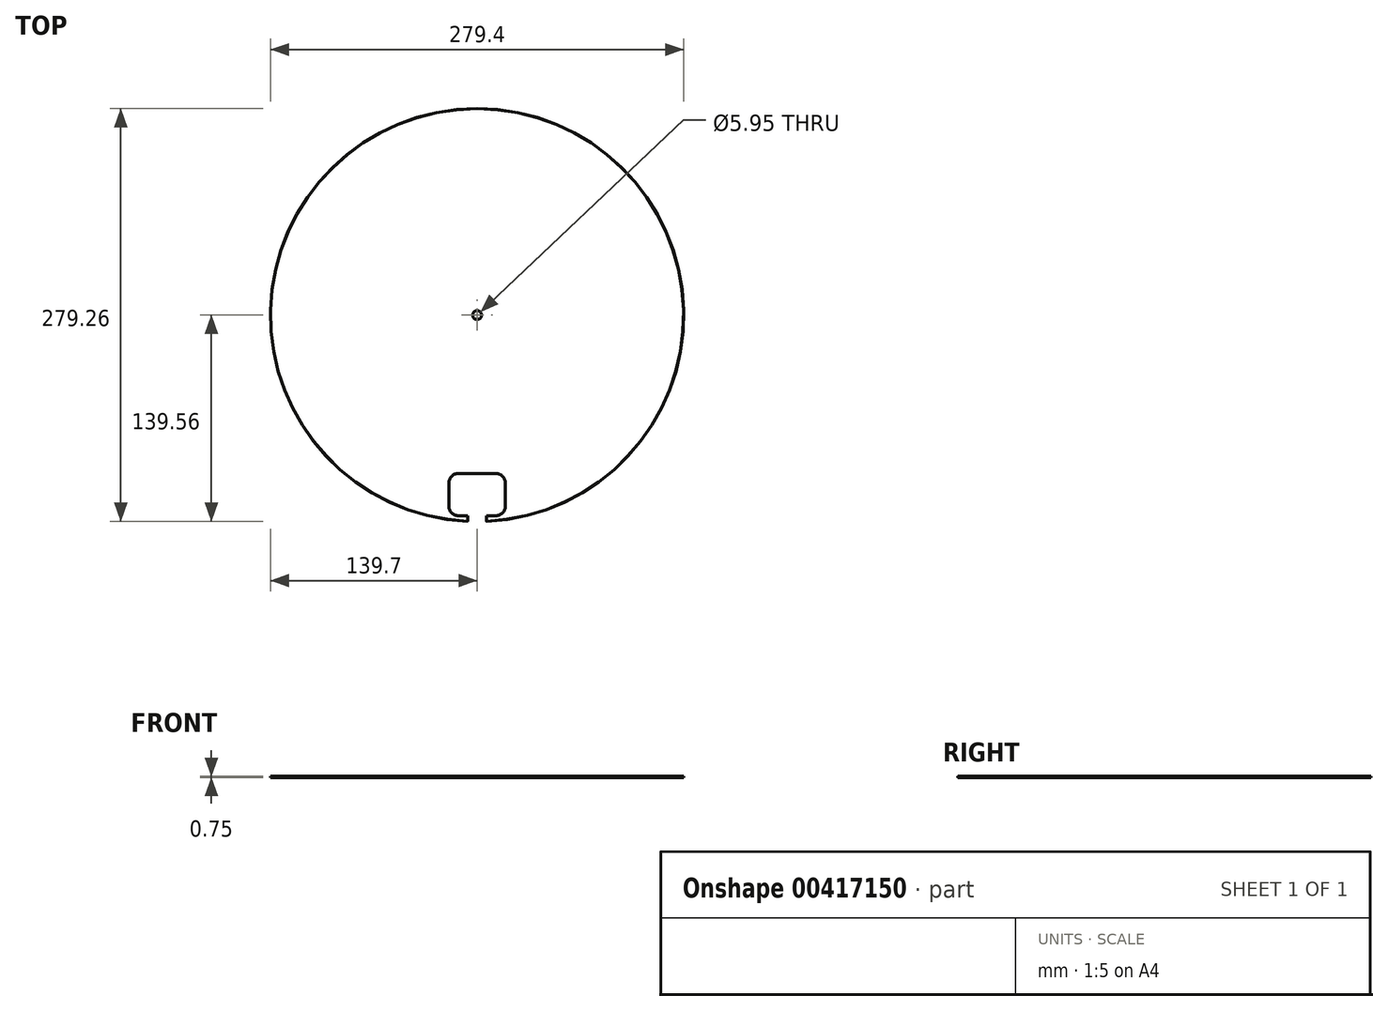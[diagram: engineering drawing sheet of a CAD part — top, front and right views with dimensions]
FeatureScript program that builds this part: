
annotation { "Feature Type Name" : "Feature", "Feature Type Description" : "" }
export const myFeature = defineFeature(function(context is Context, id is Id, definition is map)
    precondition{}
    {
        {
            assignVariable(context, id + "F0", {"name" : "BaseThickness", "anyValue" : 0.75});
        }
        {
            assignVariable(context, id + "F1", {"name" : "OuterChamfer", "anyValue" : 0.06});
        }
        {
            var Q0;
            Q0=qCreatedBy(makeId("Top.planeOp"),FACE);
            var sketch = newSketch(context, id + "F2", { "sketchPlane" : qUnion([Q0])});
            skCircle(sketch, "E0", {"center": v(0, 0) * mm, "radius": 139.7 * mm});
            skCircle(sketch, "E1", {"center": v(0, 0) * mm, "radius": 2.98 * mm});
            skSolve(sketch);
        }
        {
            var Q0;
            Q0 = qSketchRegion(id + "F2", true);
            extrude(context, id + "F3", {"entities" : qUnion([Q0]), "depth" : (getVariable(context, 'BaseThickness')) * mm});
        }
        {
            var Q0;
            Q0=makeQuery(id+"F3.opExtrude","CAP_EDGE",EDGE,{"disambiguationData":[OSD([sQuery(id+"F2.wireOp",EDGE,"E0")])],"isStart":false});
            var Q1;
            Q1=makeQuery(id+"F3.opExtrude","CAP_EDGE",EDGE,{"disambiguationData":[OSD([sQuery(id+"F2.wireOp",EDGE,"E0")])],"isStart":true});
            chamfer(context, id + "F4", {"entities" : qUnion([Q0, Q1]), "width" : (getVariable(context, 'OuterChamfer')) * mm, "tangentPropagation" : true});
        }
        {
            var Q0;
            Q0=makeQuery(id+"F3.opExtrude","CAP_FACE",FACE,{"disambiguationData":[OSD([sQuery(id+"F2.wireOp",EDGE,"E0"),sQuery(id+"F2.wireOp",EDGE,"E1")])],"isStart":false});
            var sketch = newSketch(context, id + "F5", { "sketchPlane" : qUnion([Q0])});
            skLineSegment(sketch, "E2", {"start": v(0, -156) * mm, "end": v(0, 153.57) * mm, "construction": true});
            skLineSegment(sketch, "E3", {"start": v(-121.04, -139.7) * mm, "end": v(146.95, -139.7) * mm, "construction": true});
            skArc(sketch, "E4", {"start": v(6.35, -114.3) * mm, "mid": v(0, -107.95) * mm, "end": v(-6.35, -114.3) * mm});
            skLineSegment(sketch, "E5.top", {"start": v(-6.35, -143.82) * mm, "end": v(6.35, -143.82) * mm});
            skLineSegment(sketch, "E5.left", {"start": v(-6.35, -114.3) * mm, "end": v(-6.35, -143.82) * mm});
            skLineSegment(sketch, "E5.right", {"start": v(6.35, -114.3) * mm, "end": v(6.35, -143.82) * mm});
            skSolve(sketch);
        }
        {
            var Q0;
            {var subQ0=sQuery(id+"F5.wireOp",EDGE,"E4");Q0=makeQuery(id+"F5.imprint","IMPRINT",FACE,{"disambiguationData":[TD([[makeQuery(id+"F5.imprint","IMPRINT",EDGE,{"derivedFrom":subQ0}),1.0]])]});}
            var Q1;
            {var subQ0=sQuery(id+"F5.wireOp",EDGE,"E5.top");Q1=makeQuery(id+"F5.imprint","IMPRINT",FACE,{"disambiguationData":[TD([[makeQuery(id+"F5.imprint","IMPRINT",EDGE,{"derivedFrom":subQ0}),1.0]])]});}
            extrude(context, id + "F6", {"entities" : qUnion([Q0, Q1]), "operationType" : NewBodyOperationType.REMOVE, "oppositeDirection" : true, "depth" : 5.56 * mm});
        }
        {
            var Q0;
            Q0=makeQuery(id+"F3.opExtrude","CAP_FACE",FACE,{"disambiguationData":[OSD([sQuery(id+"F2.wireOp",EDGE,"E0"),sQuery(id+"F2.wireOp",EDGE,"E1")])],"isStart":false});
            var sketch = newSketch(context, id + "F7", { "sketchPlane" : qUnion([Q0])});
            skLineSegment(sketch, "E6", {"start": v(0, -158.38) * mm, "end": v(0, 45.93) * mm, "construction": true});
            skLineSegment(sketch, "E7", {"start": v(-174.58, -139.7) * mm, "end": v(193.64, -139.7) * mm, "construction": true});
            skLineSegment(sketch, "E8.bottom", {"start": v(-12.7, -107.16) * mm, "end": v(12.7, -107.16) * mm});
            skLineSegment(sketch, "E8.top", {"start": v(-12.7, -135.73) * mm, "end": v(12.7, -135.73) * mm});
            skLineSegment(sketch, "E8.left", {"start": v(-19.05, -113.5) * mm, "end": v(-19.05, -129.38) * mm});
            skLineSegment(sketch, "E8.right", {"start": v(19.05, -113.5) * mm, "end": v(19.05, -129.38) * mm});
            skPoint(sketch, "E9.visualSharp", {"position": v(-19.05, -135.73) * mm});
            skArc(sketch, "E9.filletArc", {"start": v(-19.05, -129.38) * mm, "mid": v(-17.2, -133.87) * mm, "end": v(-12.7, -135.73) * mm});
            skPoint(sketch, "E10.visualSharp", {"position": v(19.05, -135.73) * mm});
            skArc(sketch, "E10.filletArc", {"start": v(12.7, -135.73) * mm, "mid": v(17.2, -133.87) * mm, "end": v(19.05, -129.38) * mm});
            skPoint(sketch, "E11.visualSharp", {"position": v(19.05, -107.16) * mm});
            skArc(sketch, "E11.filletArc", {"start": v(19.05, -113.5) * mm, "mid": v(17.2, -109.02) * mm, "end": v(12.7, -107.16) * mm});
            skPoint(sketch, "E12.visualSharp", {"position": v(-19.05, -107.16) * mm});
            skArc(sketch, "E12.filletArc", {"start": v(-12.7, -107.16) * mm, "mid": v(-17.2, -109.02) * mm, "end": v(-19.05, -113.5) * mm});
            skSolve(sketch);
        }
        {
            var Q0;
            Q0=makeQuery(id+"F7.imprint","IMPRINT",FACE,{"disambiguationData":[TD([[makeQuery(id+"F7.imprint","IMPRINT",EDGE,{"derivedFrom":sQuery(id+"F7.wireOp",EDGE,"E8.bottom")}),-1.0]])]});
            var Q1;
            {var subQ5=makeQuery(id+"F6.boolean.opBoolean","COPY",EDGE,{"derivedFrom":makeQuery(id+"F6.opExtrude","CAP_EDGE",EDGE,{"disambiguationData":[OSD([sQuery(id+"F5.wireOp",EDGE,"E4")])],"isStart":true})});Q1=makeQuery(id+"F7.imprint","IMPRINT",FACE,{"disambiguationData":[TD([[makeQuery(id+"F7.imprint","IMPRINT",EDGE,{"derivedFrom":subQ5}),1.0]])]});}
            extrude(context, id + "F8", {"entities" : qUnion([Q0, Q1]), "operationType" : NewBodyOperationType.REMOVE, "oppositeDirection" : true, "depth" : 9.52 * mm});
        }
    });
